# Revit family: Renzo Vanguard 300x600mm Warning TGSI
name_source: partatom
category: Generic Models
units: mm (PartAtom-declared; Revit-internal decimal feet)

## family parameters
Always vertical = No
Can host rebar = No
Cut with Voids When Loaded = No
Host = Floor
Part Type = Normal
Room Calculation Point = No
Round Connector Dimension = Use Diameter
Shared = No

## types (3) — shared parameters
Description = Slip Resistance Classification: P5
Luminous Contrast Requirement (LCR): 30%
Manufacturer = Korb
URL = https://korb.au
zero-valued in all types: Default Elevation

## per-type parameters (varying)
| type | Assembly Code | Model | TGSI_Material | Type Comments |
| Renzo Vanguard 300x600 Black - Integrated Warning | SKU: 124111 | Renzo® Vanguard 300x600 Black - Integrated Warning | Opaque Black | Mean Dry Luminance (LRV): 1.36
Mean Wet Luminance (LRV): 1.85 |
| Renzo Vanguard 300x600 White - Integrated Warning | SKU: 124114 | Renzo® Vanguard 300x600 White - Integrated Warning | Opaque  White | Mean Dry Luminance (LRV): 81.98
Mean Wet Luminance (LRV): 81.43 |
| Renzo Vanguard 300x600 Yellow - Integrated Warning | SKU: 124118 | Renzo® Vanguard 300x600 Yellow - Integrated Warning | Opaque  Yellow | Mean Dry Luminance (LRV): 63.23
Mean Wet Luminance (LRV): 63.72 |

## geometry (parser evidence)
native form markers: Sweep x13
no freeform markers — native parametric forms only
